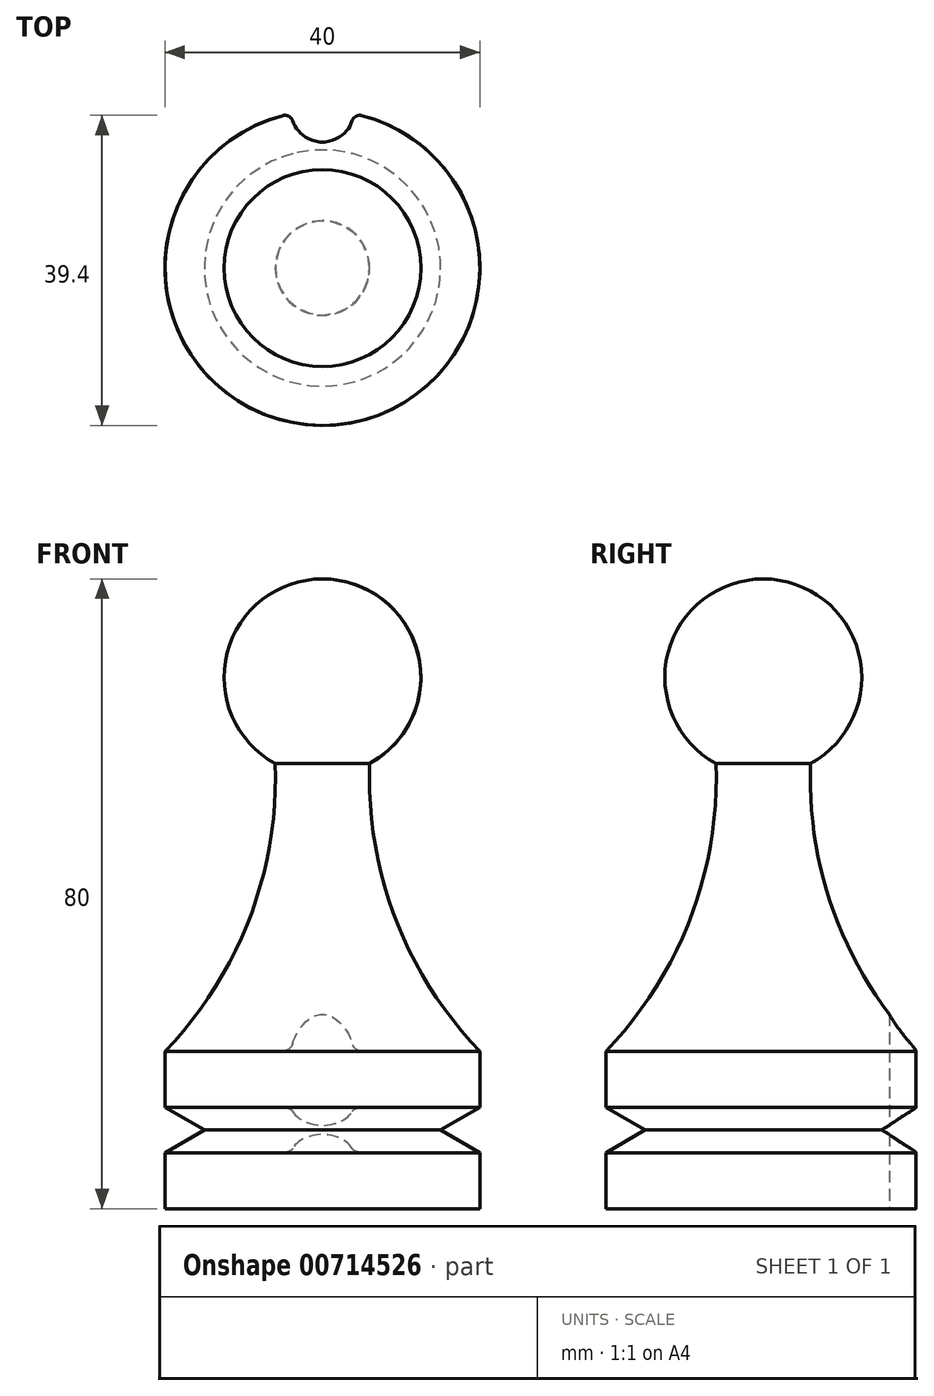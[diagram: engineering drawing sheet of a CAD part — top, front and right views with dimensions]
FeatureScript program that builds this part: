
annotation { "Feature Type Name" : "Feature", "Feature Type Description" : "" }
export const myFeature = defineFeature(function(context is Context, id is Id, definition is map)
    precondition{}
    {
        {
            var Q0;
            Q0=qCreatedBy(makeId("Front.planeOp"),FACE);
            var sketch = newSketch(context, id + "F0", { "sketchPlane" : qUnion([Q0])});
            skLineSegment(sketch, "E0", {"start": v(0, 117.58) * mm, "end": v(0, -102.12) * mm, "construction": true});
            skLineSegment(sketch, "E1", {"start": v(0, 0) * mm, "end": v(20, 0) * mm});
            skLineSegment(sketch, "E2", {"start": v(20, 0) * mm, "end": v(20, 7.11) * mm});
            skLineSegment(sketch, "E3", {"start": v(20, 7.11) * mm, "end": v(15, 10) * mm});
            skLineSegment(sketch, "E4", {"start": v(15, 10) * mm, "end": v(20, 12.89) * mm});
            skLineSegment(sketch, "E5", {"start": v(20, 12.89) * mm, "end": v(20, 20) * mm});
            skArc(sketch, "E6", {"start": v(6, 56.53) * mm, "mid": v(9.28, 36.84) * mm, "end": v(20, 20) * mm});
            skArc(sketch, "E7", {"start": v(6, 56.53) * mm, "mid": v(12.11, 70.6) * mm, "end": v(0, 80) * mm});
            skLineSegment(sketch, "E8", {"start": v(0, 80) * mm, "end": v(0, 0) * mm});
            skSolve(sketch);
        }
        {
            var Q0;
            Q0=makeQuery(id+"F0.imprint","IMPRINT",FACE,{"disambiguationData":[TD([[makeQuery(id+"F0.imprint","IMPRINT",EDGE,{"derivedFrom":sQuery(id+"F0.wireOp",EDGE,"E1")}),1.0]])]});
            var Q1;
            Q1=sQuery(id+"F0.wireOp",EDGE,"E8");
            revolve(context, id + "F1", {"surfaceOperationType" : NewSurfaceOperationType.NEW, "entities" : qUnion([Q0]), "axis" : qUnion([Q1]), "revolveType" : RevolveType.FULL});
        }
        {
            var Q0;
            Q0=makeQuery(id+"F1.opRevolve","SWEPT_FACE",FACE,{"disambiguationData":[OSD([sQuery(id+"F0.wireOp",EDGE,"E1")])]});
            var sketch = newSketch(context, id + "F2", { "sketchPlane" : qUnion([Q0])});
            skCircle(sketch, "E9", {"center": v(0, -20) * mm, "radius": 4 * mm});
            skSolve(sketch);
        }
        {
            var Q0;
            {var subQ0=sQuery(id+"F2.wireOp",EDGE,"E9");var subQ1=makeQuery(id+"F1.opRevolve","SWEPT_EDGE",EDGE,{"disambiguationData":[OSD([sQuery(id+"F0.wireOp",EDGE,"E1"),sQuery(id+"F0.wireOp",EDGE,"E2")])]});var subQ2=makeQuery(id+"F2.imprint","INTERSECT",VERTEX,{"disambiguationData":[OD(0.0)],"derivedFrom":[subQ1,subQ0]});Q0=makeQuery(id+"F2.imprint","IMPRINT",FACE,{"disambiguationData":[TD([[makeQuery(id+"F2.imprint","IMPRINT",EDGE,{"disambiguationData":[TD([[subQ2,-1.0]])],"derivedFrom":subQ0}),1.0]])]});}
            var Q1;
            {var subQ0=sQuery(id+"F2.wireOp",EDGE,"E9");var subQ1=makeQuery(id+"F1.opRevolve","SWEPT_EDGE",EDGE,{"disambiguationData":[OSD([sQuery(id+"F0.wireOp",EDGE,"E1"),sQuery(id+"F0.wireOp",EDGE,"E2")])]});var subQ2=makeQuery(id+"F2.imprint","INTERSECT",VERTEX,{"disambiguationData":[OD(0.0)],"derivedFrom":[subQ1,subQ0]});Q1=makeQuery(id+"F2.imprint","IMPRINT",FACE,{"disambiguationData":[TD([[makeQuery(id+"F2.imprint","IMPRINT",EDGE,{"disambiguationData":[TD([[subQ2,1.0]])],"derivedFrom":subQ0}),1.0]])]});}
            extrude(context, id + "F3", {"entities" : qUnion([Q0, Q1]), "operationType" : NewBodyOperationType.REMOVE, "oppositeDirection" : true, "depth" : 25 * mm, "offsetDistance" : 25 * mm});
        }
        {
            var Q0;
            Q0=makeQuery(id+"F3.boolean.opBoolean","INTERSECT",EDGE,{"disambiguationData":[OD(1.0)],"derivedFrom":[makeQuery(id+"F1.opRevolve","SWEPT_FACE",FACE,{"disambiguationData":[OSD([sQuery(id+"F0.wireOp",EDGE,"E5")])]}),makeQuery(id+"F3.opExtrude","SWEPT_FACE",FACE,{"disambiguationData":[OSD([sQuery(id+"F2.wireOp",EDGE,"E9")])]})]});
            var Q1;
            Q1=makeQuery(id+"F3.boolean.opBoolean","INTERSECT",EDGE,{"disambiguationData":[OD(0.0)],"derivedFrom":[makeQuery(id+"F1.opRevolve","SWEPT_FACE",FACE,{"disambiguationData":[OSD([sQuery(id+"F0.wireOp",EDGE,"E5")])]}),makeQuery(id+"F3.opExtrude","SWEPT_FACE",FACE,{"disambiguationData":[OSD([sQuery(id+"F2.wireOp",EDGE,"E9")])]})]});
            var Q2;
            Q2=makeQuery(id+"F3.boolean.opBoolean","INTERSECT",EDGE,{"disambiguationData":[OD(1.0)],"derivedFrom":[makeQuery(id+"F1.opRevolve","SWEPT_FACE",FACE,{"disambiguationData":[OSD([sQuery(id+"F0.wireOp",EDGE,"E2")])]}),makeQuery(id+"F3.opExtrude","SWEPT_FACE",FACE,{"disambiguationData":[OSD([sQuery(id+"F2.wireOp",EDGE,"E9")])]})]});
            var Q3;
            Q3=makeQuery(id+"F3.boolean.opBoolean","INTERSECT",EDGE,{"disambiguationData":[OD(0.0)],"derivedFrom":[makeQuery(id+"F1.opRevolve","SWEPT_FACE",FACE,{"disambiguationData":[OSD([sQuery(id+"F0.wireOp",EDGE,"E2")])]}),makeQuery(id+"F3.opExtrude","SWEPT_FACE",FACE,{"disambiguationData":[OSD([sQuery(id+"F2.wireOp",EDGE,"E9")])]})]});
            fillet(context, id + "F4", {"entities" : qUnion([Q0, Q1, Q2, Q3]), "radius" : 1 * mm, "tangentPropagation" : true, "allowEdgeOverflow" : false});
        }
    });
